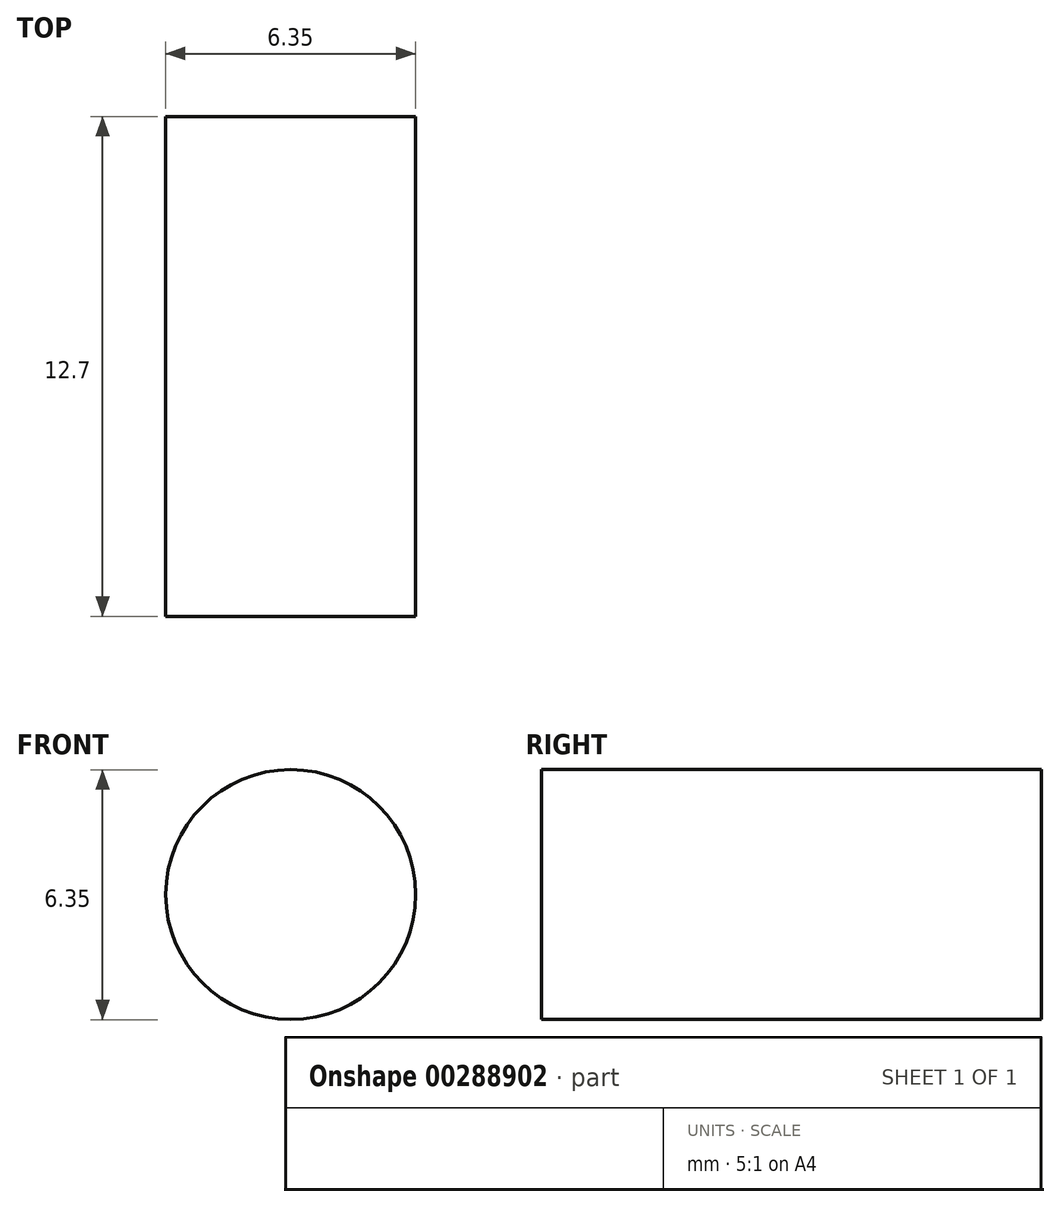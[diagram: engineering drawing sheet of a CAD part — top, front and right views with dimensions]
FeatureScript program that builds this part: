
annotation { "Feature Type Name" : "Feature", "Feature Type Description" : "" }
export const myFeature = defineFeature(function(context is Context, id is Id, definition is map)
    precondition{}
    {
        {
            var Q0;
            Q0=qCreatedBy(makeId("Front.planeOp"),FACE);
            var sketch = newSketch(context, id + "F0", { "sketchPlane" : qUnion([Q0])});
            skCircle(sketch, "E0", {"center": v(-16.98, 17.27) * mm, "radius": 3.18 * mm});
            skSolve(sketch);
        }
        {
            var Q0;
            Q0 = qSketchRegion(id + "F0", true);
            extrude(context, id + "F1", {"entities" : qUnion([Q0]), "depth" : 12.7 * mm});
        }
    });
